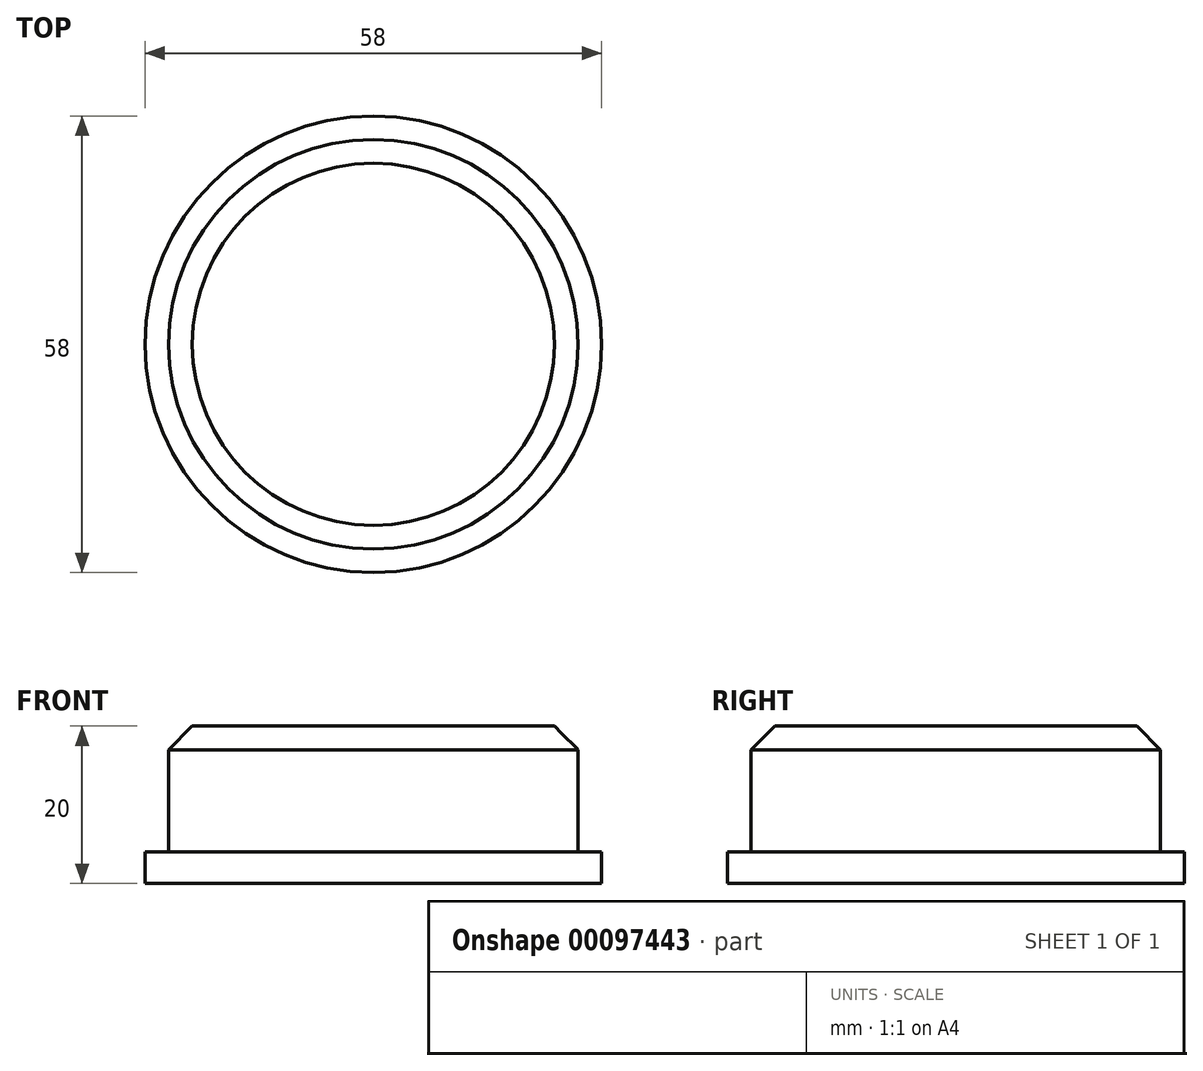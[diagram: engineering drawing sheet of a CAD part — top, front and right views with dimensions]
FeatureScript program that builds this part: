
annotation { "Feature Type Name" : "Feature", "Feature Type Description" : "" }
export const myFeature = defineFeature(function(context is Context, id is Id, definition is map)
    precondition{}
    {
        {
            var Q0;
            Q0=qCreatedBy(makeId("Top.planeOp"),FACE);
            var sketch = newSketch(context, id + "F0", { "sketchPlane" : qUnion([Q0])});
            skCircle(sketch, "E0", {"center": v(0, 0) * mm, "radius": 26 * mm});
            skLineSegment(sketch, "E1.bottom", {"start": v(7.18, -2.86) * mm, "end": v(-7.18, -2.86) * mm});
            skLineSegment(sketch, "E1.top", {"start": v(7.18, 2.86) * mm, "end": v(-7.18, 2.86) * mm});
            skLineSegment(sketch, "E1.left", {"start": v(7.18, -2.86) * mm, "end": v(7.18, 2.86) * mm});
            skLineSegment(sketch, "E1.right", {"start": v(-7.18, -2.86) * mm, "end": v(-7.18, 2.86) * mm});
            skCircle(sketch, "E2", {"center": v(0, 0) * mm, "radius": 29 * mm});
            skSolve(sketch);
        }
        {
            var Q0;
            Q0=makeQuery(id+"F0.imprint","IMPRINT",FACE,{"disambiguationData":[TD([[makeQuery(id+"F0.imprint","IMPRINT",EDGE,{"derivedFrom":sQuery(id+"F0.wireOp",EDGE,"E0")}),1.0]])]});
            var Q1;
            Q1=makeQuery(id+"F0.imprint","IMPRINT",FACE,{"disambiguationData":[TD([[makeQuery(id+"F0.imprint","IMPRINT",EDGE,{"derivedFrom":sQuery(id+"F0.wireOp",EDGE,"E1.bottom")}),-1.0]])]});
            extrude(context, id + "F1", {"entities" : qUnion([Q0, Q1]), "depth" : 20 * mm});
        }
        {
            var Q0;
            Q0=makeQuery(id+"F0.imprint","IMPRINT",FACE,{"disambiguationData":[TD([[makeQuery(id+"F0.imprint","IMPRINT",EDGE,{"derivedFrom":sQuery(id+"F0.wireOp",EDGE,"E0")}),-1.0]])]});
            extrude(context, id + "F2", {"entities" : qUnion([Q0]), "operationType" : NewBodyOperationType.ADD, "depth" : 4 * mm});
        }
        {
            var Q0;
            Q0=makeQuery(id+"F1.opExtrude","CAP_EDGE",EDGE,{"disambiguationData":[OSD([sQuery(id+"F0.wireOp",EDGE,"E0")])],"isStart":false});
            chamfer(context, id + "F3", {"entities" : qUnion([Q0]), "width" : 3 * mm, "tangentPropagation" : true});
        }
    });
